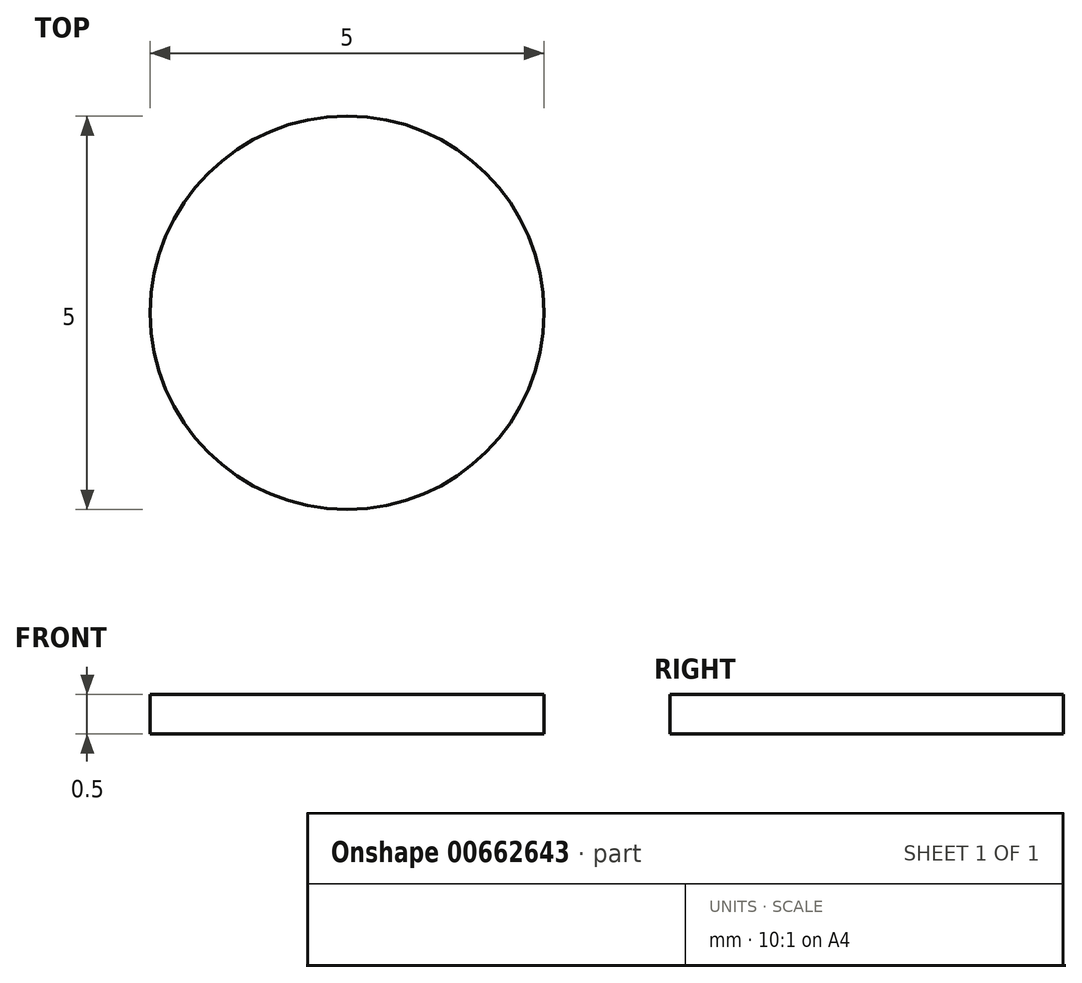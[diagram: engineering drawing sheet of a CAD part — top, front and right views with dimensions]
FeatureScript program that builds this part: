
annotation { "Feature Type Name" : "Feature", "Feature Type Description" : "" }
export const myFeature = defineFeature(function(context is Context, id is Id, definition is map)
    precondition{}
    {
        {
            var Q0;
            Q0=qCreatedBy(makeId("Top.planeOp"),FACE);
            var sketch = newSketch(context, id + "F0", { "sketchPlane" : qUnion([Q0])});
            skCircle(sketch, "E0", {"center": v(0, 0) * mm, "radius": 2.5 * mm});
            skSolve(sketch);
        }
        {
            var Q0;
            Q0 = qSketchRegion(id + "F0", true);
            extrude(context, id + "F1", {"entities" : qUnion([Q0]), "depth" : .5 * mm, "offsetDistance" : 25 * mm});
        }
    });
